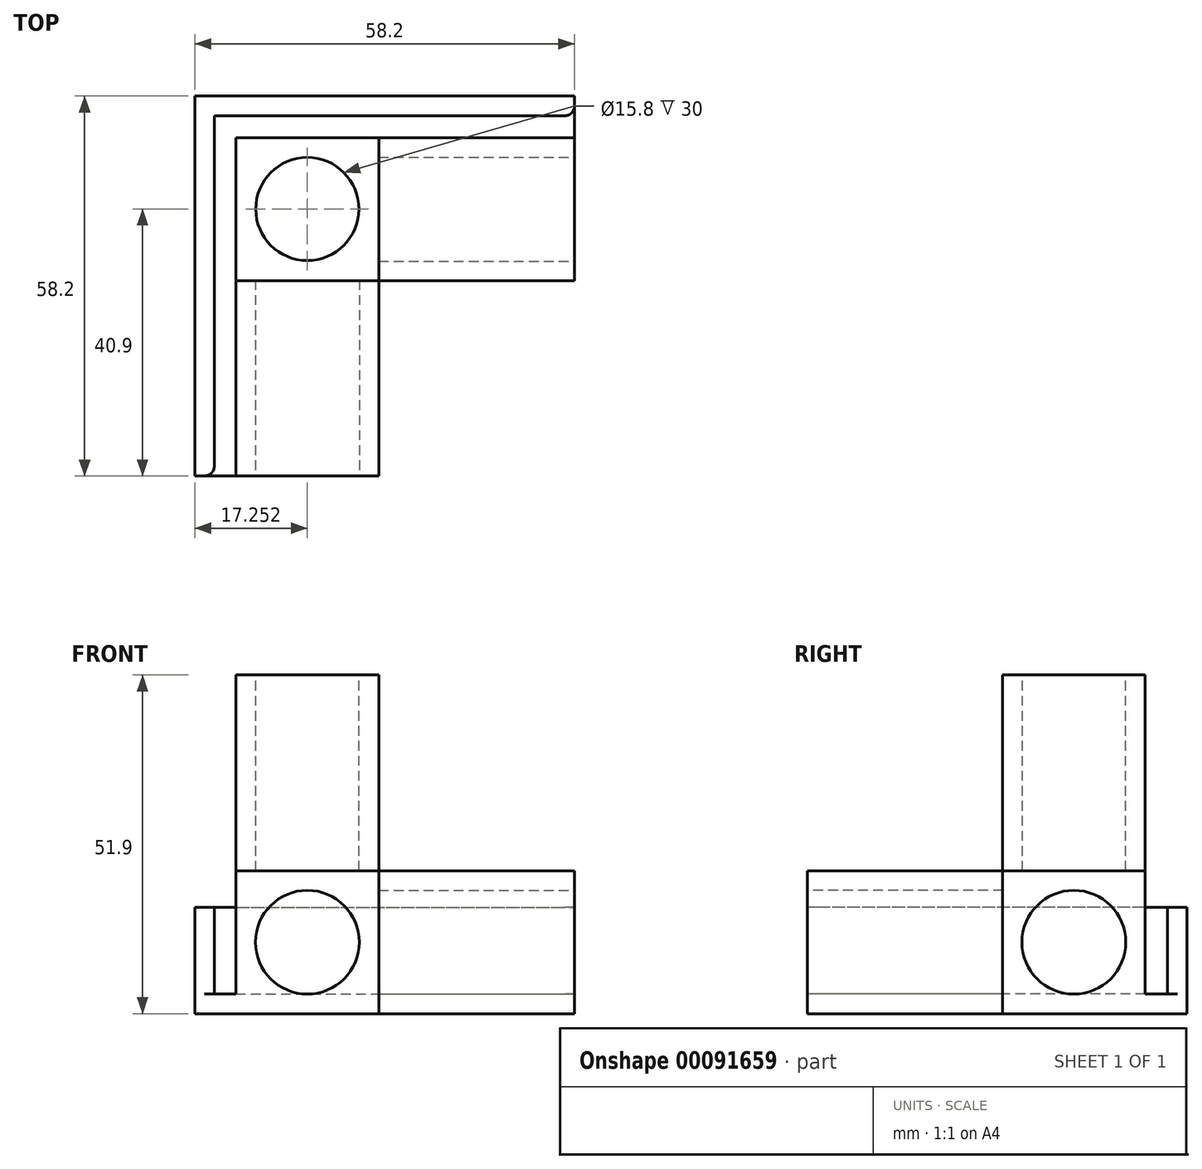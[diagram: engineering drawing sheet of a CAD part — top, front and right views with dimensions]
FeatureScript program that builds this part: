
annotation { "Feature Type Name" : "Feature", "Feature Type Description" : "" }
export const myFeature = defineFeature(function(context is Context, id is Id, definition is map)
    precondition{}
    {
        {
            var Q0;
            Q0=qCreatedBy(makeId("Front.planeOp"),FACE);
            var sketch = newSketch(context, id + "F0", { "sketchPlane" : qUnion([Q0])});
            skLineSegment(sketch, "E0.bottom", {"start": v(-42.3, 45.9) * mm, "end": v(-26.4, 45.9) * mm});
            skLineSegment(sketch, "E0.top", {"start": v(-42.3, 0) * mm, "end": v(-26.4, 0) * mm});
            skLineSegment(sketch, "E0.left", {"start": v(-42.3, 45.9) * mm, "end": v(-42.3, 0) * mm});
            skLineSegment(sketch, "E0.right", {"start": v(-26.4, 45.9) * mm, "end": v(-26.4, 15.9) * mm});
            skLineSegment(sketch, "E1.top", {"start": v(-42.3, 15.9) * mm, "end": v(-26.4, 15.9) * mm});
            skLineSegment(sketch, "E1.left", {"start": v(-42.3, 0) * mm, "end": v(-42.3, 15.9) * mm});
            skLineSegment(sketch, "E1.right", {"start": v(3.6, 0) * mm, "end": v(3.6, 15.9) * mm});
            skLineSegment(sketch, "E2", {"start": v(-26.4, 15.9) * mm, "end": v(-26.4, 0) * mm});
            skLineSegment(sketch, "E3", {"start": v(-26.4, 15.9) * mm, "end": v(3.6, 15.9) * mm});
            skLineSegment(sketch, "E4", {"start": v(-26.4, 0) * mm, "end": v(-26.4, 0) * mm});
            skLineSegment(sketch, "E5", {"start": v(-42.3, 15.9) * mm, "end": v(-42.3, 15.9) * mm});
            skLineSegment(sketch, "E6", {"start": v(-26.4, 0) * mm, "end": v(3.6, 0) * mm});
            skLineSegment(sketch, "E7.0", {"start": v(-45.3, 48.9) * mm, "end": v(-45.3, -3) * mm});
            skLineSegment(sketch, "E7.1", {"start": v(-45.3, -3) * mm, "end": v(-23.4, -3) * mm});
            skLineSegment(sketch, "E7.2", {"start": v(-23.4, 48.9) * mm, "end": v(-23.4, 18.9) * mm});
            skLineSegment(sketch, "E7.3", {"start": v(-23.4, 18.9) * mm, "end": v(6.6, 18.9) * mm});
            skLineSegment(sketch, "E7.4", {"start": v(6.6, -3) * mm, "end": v(6.6, 18.9) * mm});
            skLineSegment(sketch, "E7.5", {"start": v(-45.3, 48.9) * mm, "end": v(-23.4, 48.9) * mm});
            skLineSegment(sketch, "E7.6", {"start": v(-23.4, -3) * mm, "end": v(6.6, -3) * mm});
            skPoint(sketch, "E8", {"position": v(-34.36, 7.95) * mm});
            skPoint(sketch, "E8.positionSnap0", {"position": v(-26.4, 7.95) * mm});
            skPoint(sketch, "E8.positionSnap1", {"position": v(-34.36, 15.9) * mm});
            skCircle(sketch, "E9", {"center": v(-34.36, 7.95) * mm, "radius": 7.95 * mm});
            skLineSegment(sketch, "E10", {"start": v(-23.4, 18.9) * mm, "end": v(-45.3, 18.9) * mm});
            skLineSegment(sketch, "E11", {"start": v(-23.4, 18.9) * mm, "end": v(-23.4, -3) * mm});
            skSolve(sketch);
        }
        {
            var Q0;
            {var subQ1=sQuery(id+"F0.wireOp",EDGE,"E1.top");var subQ3=sQuery(id+"F0.wireOp",EDGE,"E9");var subQ4=makeQuery(id+"F0.imprint","INTERSECT",VERTEX,{"derivedFrom":[subQ1,subQ3]});Q0=makeQuery(id+"F0.imprint","IMPRINT",FACE,{"disambiguationData":[TD([[makeQuery(id+"F0.imprint","IMPRINT",EDGE,{"disambiguationData":[TD([[subQ4,-1.0]])],"derivedFrom":subQ3}),-1.0]])]});}
            var Q1;
            {var subQ0=sQuery(id+"F0.wireOp",EDGE,"E9");var subQ1=makeQuery(id+"F0.imprint","INTERSECT",VERTEX,{"derivedFrom":[sQuery(id+"F0.wireOp",EDGE,"E1.top"),subQ0]});Q1=makeQuery(id+"F0.imprint","IMPRINT",FACE,{"disambiguationData":[TD([[makeQuery(id+"F0.imprint","IMPRINT",EDGE,{"disambiguationData":[TD([[subQ1,1.0]])],"derivedFrom":subQ0}),1.0]])]});}
            var Q2;
            {var subQ5=sQuery(id+"F0.wireOp",EDGE,"E0.bottom");Q2=makeQuery(id+"F0.imprint","IMPRINT",FACE,{"disambiguationData":[TD([[makeQuery(id+"F0.imprint","IMPRINT",EDGE,{"derivedFrom":subQ5}),1.0]])]});}
            var Q3;
            {var subQ0=sQuery(id+"F0.wireOp",EDGE,"E1.right");Q3=makeQuery(id+"F0.imprint","IMPRINT",FACE,{"disambiguationData":[TD([[makeQuery(id+"F0.imprint","IMPRINT",EDGE,{"derivedFrom":subQ0}),1.0]])]});}
            var Q4;
            {var subQ0=sQuery(id+"F0.wireOp",EDGE,"E0.bottom");Q4=makeQuery(id+"F0.imprint","IMPRINT",FACE,{"disambiguationData":[TD([[makeQuery(id+"F0.imprint","IMPRINT",EDGE,{"derivedFrom":subQ0}),-1.0]])]});}
            var Q5;
            {var subQ0=sQuery(id+"F0.wireOp",EDGE,"E1.left");var subQ1=sQuery(id+"F0.wireOp",EDGE,"E0.top");var subQ2=makeQuery(id+"F0.imprint","INTERSECT",VERTEX,{"derivedFrom":[subQ1,subQ0]});Q5=makeQuery(id+"F0.imprint","IMPRINT",FACE,{"disambiguationData":[TD([[makeQuery(id+"F0.imprint","IMPRINT",EDGE,{"disambiguationData":[TD([[subQ2,-1.0]])],"derivedFrom":subQ1}),1.0]])]});}
            var Q6;
            {var subQ1=sQuery(id+"F0.wireOp",EDGE,"E0.top");var subQ3=sQuery(id+"F0.wireOp",EDGE,"E9");var subQ4=makeQuery(id+"F0.imprint","INTERSECT",VERTEX,{"derivedFrom":[subQ1,subQ3]});Q6=makeQuery(id+"F0.imprint","IMPRINT",FACE,{"disambiguationData":[TD([[makeQuery(id+"F0.imprint","IMPRINT",EDGE,{"disambiguationData":[TD([[subQ4,-1.0]])],"derivedFrom":subQ3}),-1.0]])]});}
            var Q7;
            {var subQ1=sQuery(id+"F0.wireOp",EDGE,"E1.top");var subQ3=sQuery(id+"F0.wireOp",EDGE,"E9");var subQ4=makeQuery(id+"F0.imprint","INTERSECT",VERTEX,{"derivedFrom":[subQ1,subQ3]});Q7=makeQuery(id+"F0.imprint","IMPRINT",FACE,{"disambiguationData":[TD([[makeQuery(id+"F0.imprint","IMPRINT",EDGE,{"disambiguationData":[TD([[subQ4,1.0]])],"derivedFrom":subQ3}),-1.0]])]});}
            var Q8;
            {var subQ5=sQuery(id+"F0.wireOp",EDGE,"E1.right");Q8=makeQuery(id+"F0.imprint","IMPRINT",FACE,{"disambiguationData":[TD([[makeQuery(id+"F0.imprint","IMPRINT",EDGE,{"derivedFrom":subQ5}),-1.0]])]});}
            var Q9;
            {var subQ4=sQuery(id+"F0.wireOp",EDGE,"E0.left");var subQ6=sQuery(id+"F0.wireOp",EDGE,"E10");var subQ8=makeQuery(id+"F0.imprint","INTERSECT",VERTEX,{"derivedFrom":[subQ4,subQ6]});Q9=makeQuery(id+"F0.imprint","IMPRINT",FACE,{"disambiguationData":[TD([[makeQuery(id+"F0.imprint","IMPRINT",EDGE,{"disambiguationData":[TD([[subQ8,1.0]])],"derivedFrom":subQ6}),1.0]])]});}
            var Q10;
            {var subQ3=sQuery(id+"F0.wireOp",EDGE,"E11");var subQ5=sQuery(id+"F0.wireOp",EDGE,"E3");var subQ8=makeQuery(id+"F0.imprint","INTERSECT",VERTEX,{"derivedFrom":[subQ5,subQ3]});Q10=makeQuery(id+"F0.imprint","IMPRINT",FACE,{"disambiguationData":[TD([[makeQuery(id+"F0.imprint","IMPRINT",EDGE,{"disambiguationData":[TD([[subQ8,-1.0]])],"derivedFrom":subQ3}),-1.0]])]});}
            var Q11;
            {var subQ14=sQuery(id+"F0.wireOp",EDGE,"E7.1");Q11=makeQuery(id+"F0.imprint","IMPRINT",FACE,{"disambiguationData":[TD([[makeQuery(id+"F0.imprint","IMPRINT",EDGE,{"derivedFrom":subQ14}),1.0]])]});}
            var Q12;
            {var subQ1=sQuery(id+"F0.wireOp",EDGE,"E0.right");var subQ3=sQuery(id+"F0.wireOp",EDGE,"E10");var subQ4=makeQuery(id+"F0.imprint","INTERSECT",VERTEX,{"derivedFrom":[subQ1,subQ3]});Q12=makeQuery(id+"F0.imprint","IMPRINT",FACE,{"disambiguationData":[TD([[makeQuery(id+"F0.imprint","IMPRINT",EDGE,{"disambiguationData":[TD([[subQ4,-1.0]])],"derivedFrom":subQ1}),1.0]])]});}
            extrude(context, id + "F1", {"entities" : qUnion([Q0, Q1, Q2, Q3, Q4, Q5, Q6, Q7, Q8, Q9, Q10, Q11, Q12]), "depth" : (15.9 + 6) * mm});
        }
        {
            var Q0;
            {var subQ14=sQuery(id+"F0.wireOp",EDGE,"E7.1");Q0=makeQuery(id+"F0.imprint","IMPRINT",FACE,{"disambiguationData":[TD([[makeQuery(id+"F0.imprint","IMPRINT",EDGE,{"derivedFrom":subQ14}),1.0]])]});}
            var Q1;
            {var subQ0=sQuery(id+"F0.wireOp",EDGE,"E9");var subQ1=makeQuery(id+"F0.imprint","INTERSECT",VERTEX,{"derivedFrom":[sQuery(id+"F0.wireOp",EDGE,"E1.top"),subQ0]});Q1=makeQuery(id+"F0.imprint","IMPRINT",FACE,{"disambiguationData":[TD([[makeQuery(id+"F0.imprint","IMPRINT",EDGE,{"disambiguationData":[TD([[subQ1,1.0]])],"derivedFrom":subQ0}),1.0]])]});}
            var Q2;
            {var subQ4=sQuery(id+"F0.wireOp",EDGE,"E0.left");var subQ6=sQuery(id+"F0.wireOp",EDGE,"E10");var subQ8=makeQuery(id+"F0.imprint","INTERSECT",VERTEX,{"derivedFrom":[subQ4,subQ6]});Q2=makeQuery(id+"F0.imprint","IMPRINT",FACE,{"disambiguationData":[TD([[makeQuery(id+"F0.imprint","IMPRINT",EDGE,{"disambiguationData":[TD([[subQ8,1.0]])],"derivedFrom":subQ6}),1.0]])]});}
            var Q3;
            {var subQ3=sQuery(id+"F0.wireOp",EDGE,"E11");var subQ5=sQuery(id+"F0.wireOp",EDGE,"E3");var subQ8=makeQuery(id+"F0.imprint","INTERSECT",VERTEX,{"derivedFrom":[subQ5,subQ3]});Q3=makeQuery(id+"F0.imprint","IMPRINT",FACE,{"disambiguationData":[TD([[makeQuery(id+"F0.imprint","IMPRINT",EDGE,{"disambiguationData":[TD([[subQ8,-1.0]])],"derivedFrom":subQ3}),-1.0]])]});}
            var Q4;
            {var subQ1=sQuery(id+"F0.wireOp",EDGE,"E0.right");var subQ3=sQuery(id+"F0.wireOp",EDGE,"E10");var subQ4=makeQuery(id+"F0.imprint","INTERSECT",VERTEX,{"derivedFrom":[subQ1,subQ3]});Q4=makeQuery(id+"F0.imprint","IMPRINT",FACE,{"disambiguationData":[TD([[makeQuery(id+"F0.imprint","IMPRINT",EDGE,{"disambiguationData":[TD([[subQ4,-1.0]])],"derivedFrom":subQ1}),1.0]])]});}
            var Q5;
            {var subQ1=sQuery(id+"F0.wireOp",EDGE,"E1.top");var subQ3=sQuery(id+"F0.wireOp",EDGE,"E9");var subQ4=makeQuery(id+"F0.imprint","INTERSECT",VERTEX,{"derivedFrom":[subQ1,subQ3]});Q5=makeQuery(id+"F0.imprint","IMPRINT",FACE,{"disambiguationData":[TD([[makeQuery(id+"F0.imprint","IMPRINT",EDGE,{"disambiguationData":[TD([[subQ4,1.0]])],"derivedFrom":subQ3}),-1.0]])]});}
            var Q6;
            {var subQ1=sQuery(id+"F0.wireOp",EDGE,"E1.top");var subQ3=sQuery(id+"F0.wireOp",EDGE,"E9");var subQ4=makeQuery(id+"F0.imprint","INTERSECT",VERTEX,{"derivedFrom":[subQ1,subQ3]});Q6=makeQuery(id+"F0.imprint","IMPRINT",FACE,{"disambiguationData":[TD([[makeQuery(id+"F0.imprint","IMPRINT",EDGE,{"disambiguationData":[TD([[subQ4,-1.0]])],"derivedFrom":subQ3}),-1.0]])]});}
            var Q7;
            {var subQ0=sQuery(id+"F0.wireOp",EDGE,"E1.left");var subQ1=sQuery(id+"F0.wireOp",EDGE,"E0.top");var subQ2=makeQuery(id+"F0.imprint","INTERSECT",VERTEX,{"derivedFrom":[subQ1,subQ0]});Q7=makeQuery(id+"F0.imprint","IMPRINT",FACE,{"disambiguationData":[TD([[makeQuery(id+"F0.imprint","IMPRINT",EDGE,{"disambiguationData":[TD([[subQ2,-1.0]])],"derivedFrom":subQ1}),1.0]])]});}
            var Q8;
            {var subQ1=sQuery(id+"F0.wireOp",EDGE,"E0.top");var subQ3=sQuery(id+"F0.wireOp",EDGE,"E9");var subQ4=makeQuery(id+"F0.imprint","INTERSECT",VERTEX,{"derivedFrom":[subQ1,subQ3]});Q8=makeQuery(id+"F0.imprint","IMPRINT",FACE,{"disambiguationData":[TD([[makeQuery(id+"F0.imprint","IMPRINT",EDGE,{"disambiguationData":[TD([[subQ4,-1.0]])],"derivedFrom":subQ3}),-1.0]])]});}
            extrude(context, id + "F2", {"entities" : qUnion([Q0, Q1, Q2, Q3, Q4, Q5, Q6, Q7, Q8]), "operationType" : NewBodyOperationType.ADD, "depth" : (15.8 + 6 + 30) * mm});
        }
        {
            var Q0;
            Q0=makeQuery(id+"F2.opExtrude","CAP_FACE",FACE,{"disambiguationData":[OSD([sQuery(id+"F0.wireOp",EDGE,"E7.0"),sQuery(id+"F0.wireOp",EDGE,"E7.1"),sQuery(id+"F0.wireOp",EDGE,"E10"),sQuery(id+"F0.wireOp",EDGE,"E11")])],"isStart":false});
            var sketch = newSketch(context, id + "F3", { "sketchPlane" : qUnion([Q0])});
            skCircle(sketch, "E12.0", {"center": v(-34.36, 7.95) * mm, "radius": 7.95 * mm});
            skSolve(sketch);
        }
        {
            var Q0;
            Q0=makeQuery(id+"F1.opExtrude","SWEPT_FACE",FACE,{"disambiguationData":[OSD([sQuery(id+"F0.wireOp",EDGE,"E7.5")])]});
            var sketch = newSketch(context, id + "F4", { "sketchPlane" : qUnion([Q0])});
            skPoint(sketch, "E13", {"position": v(-34.36, -3) * mm});
            skPoint(sketch, "E14", {"position": v(-26.4, -10.9) * mm});
            skPoint(sketch, "E15", {"position": v(-34.36, -10.9) * mm});
            skPoint(sketch, "E16", {"position": v(-62.98, 75) * mm});
            skPoint(sketch, "E17.orphan", {"position": v(-42.3, -3) * mm});
            skPoint(sketch, "E18.orphan", {"position": v(-26.4, -3) * mm});
            skPoint(sketch, "E19.orphan", {"position": v(-26.4, -18.8) * mm});
            skCircle(sketch, "E20", {"center": v(-34.36, -10.9) * mm, "radius": 7.9 * mm});
            skSolve(sketch);
        }
        {
            var Q0;
            Q0=makeQuery(id+"F1.opExtrude","SWEPT_FACE",FACE,{"disambiguationData":[OSD([sQuery(id+"F0.wireOp",EDGE,"E7.4")])]});
            var sketch = newSketch(context, id + "F5", { "sketchPlane" : qUnion([Q0])});
            skLineSegment(sketch, "E21.0", {"start": v(-18.9, 15.9) * mm, "end": v(-3, 15.9) * mm});
            skLineSegment(sketch, "E21.1", {"start": v(-18.9, 0) * mm, "end": v(-18.9, 15.9) * mm});
            skLineSegment(sketch, "E21.2", {"start": v(-18.9, 0) * mm, "end": v(-3, 0) * mm});
            skLineSegment(sketch, "E21.3", {"start": v(-3, 0) * mm, "end": v(-3, 15.9) * mm});
            skCircle(sketch, "E22", {"center": v(-10.95, 7.95) * mm, "radius": 7.95 * mm});
            skPoint(sketch, "E22.centerSnap0", {"position": v(-10.95, 0) * mm});
            skPoint(sketch, "E22.centerSnap1", {"position": v(-3, 7.95) * mm});
            skSolve(sketch);
        }
        {
            var Q0;
            Q0=makeQuery(id+"F3.imprint","IMPRINT",FACE,{"disambiguationData":[TD([[makeQuery(id+"F3.imprint","IMPRINT",EDGE,{"derivedFrom":sQuery(id+"F3.wireOp",EDGE,"E12.0")}),1.0]])]});
            extrude(context, id + "F6", {"entities" : qUnion([Q0]), "operationType" : NewBodyOperationType.REMOVE, "oppositeDirection" : true, "depth" : 30 * mm});
        }
        {
            var Q0;
            {var subQ0=sQuery(id+"F5.wireOp",EDGE,"E22");var subQ1=makeQuery(id+"F5.imprint","INTERSECT",VERTEX,{"derivedFrom":[sQuery(id+"F5.wireOp",EDGE,"E21.1"),subQ0]});Q0=makeQuery(id+"F5.imprint","IMPRINT",FACE,{"disambiguationData":[TD([[makeQuery(id+"F5.imprint","IMPRINT",EDGE,{"disambiguationData":[TD([[subQ1,1.0]])],"derivedFrom":subQ0}),1.0]])]});}
            extrude(context, id + "F7", {"entities" : qUnion([Q0]), "operationType" : NewBodyOperationType.REMOVE, "oppositeDirection" : true, "depth" : 30 * mm});
        }
        {
            var Q0;
            Q0=makeQuery(id+"F4.imprint","IMPRINT",FACE,{"disambiguationData":[TD([[makeQuery(id+"F4.imprint","IMPRINT",EDGE,{"derivedFrom":sQuery(id+"F4.wireOp",EDGE,"E20")}),1.0]])]});
            var Q1;
            Q1=sQuery(id+"F4.wireOp",EDGE,"E20");
            extrude(context, id + "F8", {"entities" : qUnion([Q0]), "operationType" : NewBodyOperationType.REMOVE, "surfaceEntities" : qUnion([Q1]), "oppositeDirection" : true, "depth" : 30 * mm});
        }
        {
            var Q0;
            Q0=makeQuery(id+"F2.opExtrude","CAP_FACE",FACE,{"disambiguationData":[OSD([sQuery(id+"F0.wireOp",EDGE,"E7.0"),sQuery(id+"F0.wireOp",EDGE,"E7.1"),sQuery(id+"F0.wireOp",EDGE,"E10"),sQuery(id+"F0.wireOp",EDGE,"E11")])],"isStart":false});
            var sketch = newSketch(context, id + "F9", { "sketchPlane" : qUnion([Q0])});
            skLineSegment(sketch, "E23", {"start": v(-45.3, -3) * mm, "end": v(-51.6, -3) * mm});
            skLineSegment(sketch, "E24", {"start": v(-51.6, -3) * mm, "end": v(-51.6, 13.3) * mm});
            skLineSegment(sketch, "E25", {"start": v(-51.6, 13.3) * mm, "end": v(-48.6, 13.3) * mm});
            skLineSegment(sketch, "E26", {"start": v(-48.6, 13.3) * mm, "end": v(-48.6, 0) * mm});
            skLineSegment(sketch, "E27", {"start": v(-48.6, 0) * mm, "end": v(-45.3, 0) * mm});
            skSolve(sketch);
        }
        {
            var Q0;
            {var subQ0=sQuery(id+"F9.wireOp",EDGE,"E23");Q0=makeQuery(id+"F9.imprint","IMPRINT",FACE,{"disambiguationData":[TD([[makeQuery(id+"F9.imprint","IMPRINT",EDGE,{"derivedFrom":subQ0}),-1.0]])]});}
            extrude(context, id + "F10", {"entities" : qUnion([Q0]), "operationType" : NewBodyOperationType.ADD, "oppositeDirection" : true, "depth" : (6 + 15.9 + 30 + 6.3) * mm});
        }
        {
            var Q0;
            Q0=makeQuery(id+"F1.opExtrude","SWEPT_FACE",FACE,{"disambiguationData":[OSD([sQuery(id+"F0.wireOp",EDGE,"E7.4")])]});
            var sketch = newSketch(context, id + "F11", { "sketchPlane" : qUnion([Q0])});
            skLineSegment(sketch, "E28.0.0", {"start": v(6.4, 0) * mm, "end": v(0, 0) * mm});
            skLineSegment(sketch, "E28.0.1", {"start": v(0, 0) * mm, "end": v(0, -3) * mm});
            skLineSegment(sketch, "E28.0.2", {"start": v(0, -3) * mm, "end": v(6.4, -3) * mm});
            skLineSegment(sketch, "E28.0.3", {"start": v(6.4, -3) * mm, "end": v(6.4, 0) * mm});
            skLineSegment(sketch, "E29.0", {"start": v(6.4, 13.3) * mm, "end": v(6.4, 0) * mm});
            skLineSegment(sketch, "E30", {"start": v(6.4, 13.3) * mm, "end": v(3.4, 13.3) * mm});
            skLineSegment(sketch, "E31", {"start": v(3.4, 13.3) * mm, "end": v(3.4, 0) * mm});
            skSolve(sketch);
        }
        {
            var Q0;
            Q0=qSketchRegion(id+"F11",true);
            extrude(context, id + "F12", {"entities" : qUnion([Q0]), "operationType" : NewBodyOperationType.ADD, "endBound" : BoundingType.UP_TO_NEXT, "oppositeDirection" : true, "depth" : 25 * mm});
        }
        {
            var Q0;
            Q0=makeQuery(id+"F12.opExtrude","CAP_EDGE",EDGE,{"disambiguationData":[OSD([sQuery(id+"F11.wireOp",EDGE,"E31")])],"isStart":true});
            var Q1;
            Q1=makeQuery(id+"F10.opExtrude","CAP_EDGE",EDGE,{"disambiguationData":[OSD([sQuery(id+"F9.wireOp",EDGE,"E26")])],"isStart":true});
            fillet(context, id + "F13", {"entities" : qUnion([Q0, Q1]), "radius" : 1.5 * mm, "tangentPropagation" : true, "allowEdgeOverflow" : false});
        }
    });
